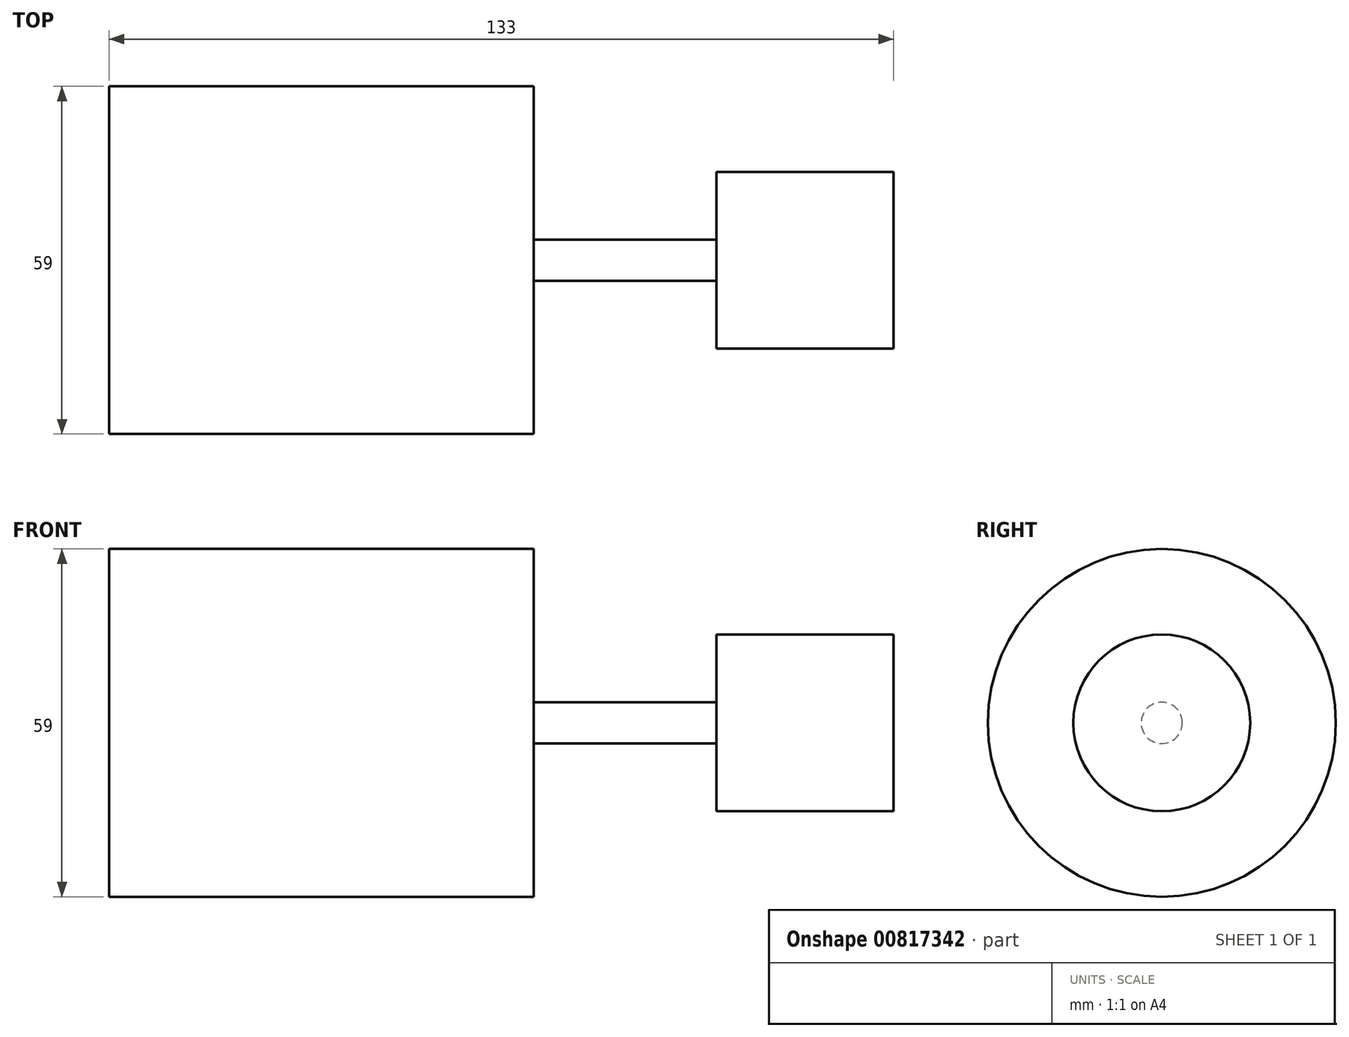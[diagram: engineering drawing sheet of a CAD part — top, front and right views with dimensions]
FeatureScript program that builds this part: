
annotation { "Feature Type Name" : "Feature", "Feature Type Description" : "" }
export const myFeature = defineFeature(function(context is Context, id is Id, definition is map)
    precondition{}
    {
        {
            var Q0;
            Q0=qCreatedBy(makeId("Top.planeOp"),FACE);
            var sketch = newSketch(context, id + "F0", { "sketchPlane" : qUnion([Q0])});
            skLineSegment(sketch, "E0.bottom", {"start": v(36, 29.5) * mm, "end": v(-36, 29.5) * mm});
            skLineSegment(sketch, "E0.top", {"start": v(36, -29.5) * mm, "end": v(-36, -29.5) * mm});
            skLineSegment(sketch, "E0.left", {"start": v(36, 29.5) * mm, "end": v(36, -29.5) * mm});
            skLineSegment(sketch, "E0.right", {"start": v(-36, 29.5) * mm, "end": v(-36, -29.5) * mm});
            skPoint(sketch, "E0.middle", {"position": v(0, 0) * mm});
            skLineSegment(sketch, "E1.bottom", {"start": v(36, 4.5) * mm, "end": v(36, 4.5) * mm});
            skLineSegment(sketch, "E1.top", {"start": v(36, -3.5) * mm, "end": v(36, -3.5) * mm});
            skLineSegment(sketch, "E1.left", {"start": v(36, 4.5) * mm, "end": v(36, -3.5) * mm});
            skLineSegment(sketch, "E1.right", {"start": v(36, 4.5) * mm, "end": v(36, -3.5) * mm});
            skLineSegment(sketch, "E2.bottom", {"start": v(36, -3.5) * mm, "end": v(67, -3.5) * mm});
            skLineSegment(sketch, "E2.top", {"start": v(36, 4.33) * mm, "end": v(67, 4.33) * mm});
            skLineSegment(sketch, "E2.left", {"start": v(36, -3.5) * mm, "end": v(36, 4.33) * mm});
            skLineSegment(sketch, "E2.right", {"start": v(67, -3.5) * mm, "end": v(67, 4.33) * mm});
            skLineSegment(sketch, "E3", {"start": v(-36, 0) * mm, "end": v(67, 0) * mm});
            skLineSegment(sketch, "E4.bottom", {"start": v(97, 15) * mm, "end": v(67, 15) * mm});
            skLineSegment(sketch, "E4.top", {"start": v(97, -15) * mm, "end": v(67, -15) * mm});
            skLineSegment(sketch, "E4.left", {"start": v(67, 15) * mm, "end": v(67, -15) * mm});
            skLineSegment(sketch, "E4.right", {"start": v(97, 15) * mm, "end": v(97, -15) * mm});
            skPoint(sketch, "E4.middle", {"position": v(82, 0) * mm});
            skLineSegment(sketch, "E5", {"start": v(67, 0) * mm, "end": v(97, 0) * mm});
            skSolve(sketch);
        }
        {
            var Q0;
            Q0=qCreatedBy(makeId("Top.planeOp"),FACE);
            var sketch = newSketch(context, id + "F1", { "sketchPlane" : qUnion([Q0])});
            skLineSegment(sketch, "E6", {"start": v(-67.97, 0) * mm, "end": v(78.74, 0) * mm});
            skSolve(sketch);
        }
        {
            var Q0;
            {var subQ3=sQuery(id+"F0.wireOp",EDGE,"E0.bottom");Q0=makeQuery(id+"F0.imprint","IMPRINT",FACE,{"disambiguationData":[TD([[makeQuery(id+"F0.imprint","IMPRINT",EDGE,{"derivedFrom":subQ3}),1.0]])]});}
            var Q1;
            Q1=makeQuery(id+"F0.imprint","IMPRINT",FACE,{"disambiguationData":[TD([[makeQuery(id+"F0.imprint","IMPRINT",EDGE,{"derivedFrom":sQuery(id+"F0.wireOp",EDGE,"E2.bottom")}),1.0]])]});
            var Q2;
            {var subQ3=sQuery(id+"F0.wireOp",EDGE,"E4.bottom");Q2=makeQuery(id+"F0.imprint","IMPRINT",FACE,{"disambiguationData":[TD([[makeQuery(id+"F0.imprint","IMPRINT",EDGE,{"derivedFrom":subQ3}),1.0]])]});}
            var Q3;
            Q3=sQuery(id+"F1.wireOp",EDGE,"E6");
            revolve(context, id + "F2", {"surfaceOperationType" : NewSurfaceOperationType.NEW, "entities" : qUnion([Q0, Q1, Q2]), "axis" : qUnion([Q3]), "revolveType" : RevolveType.FULL});
        }
    });
